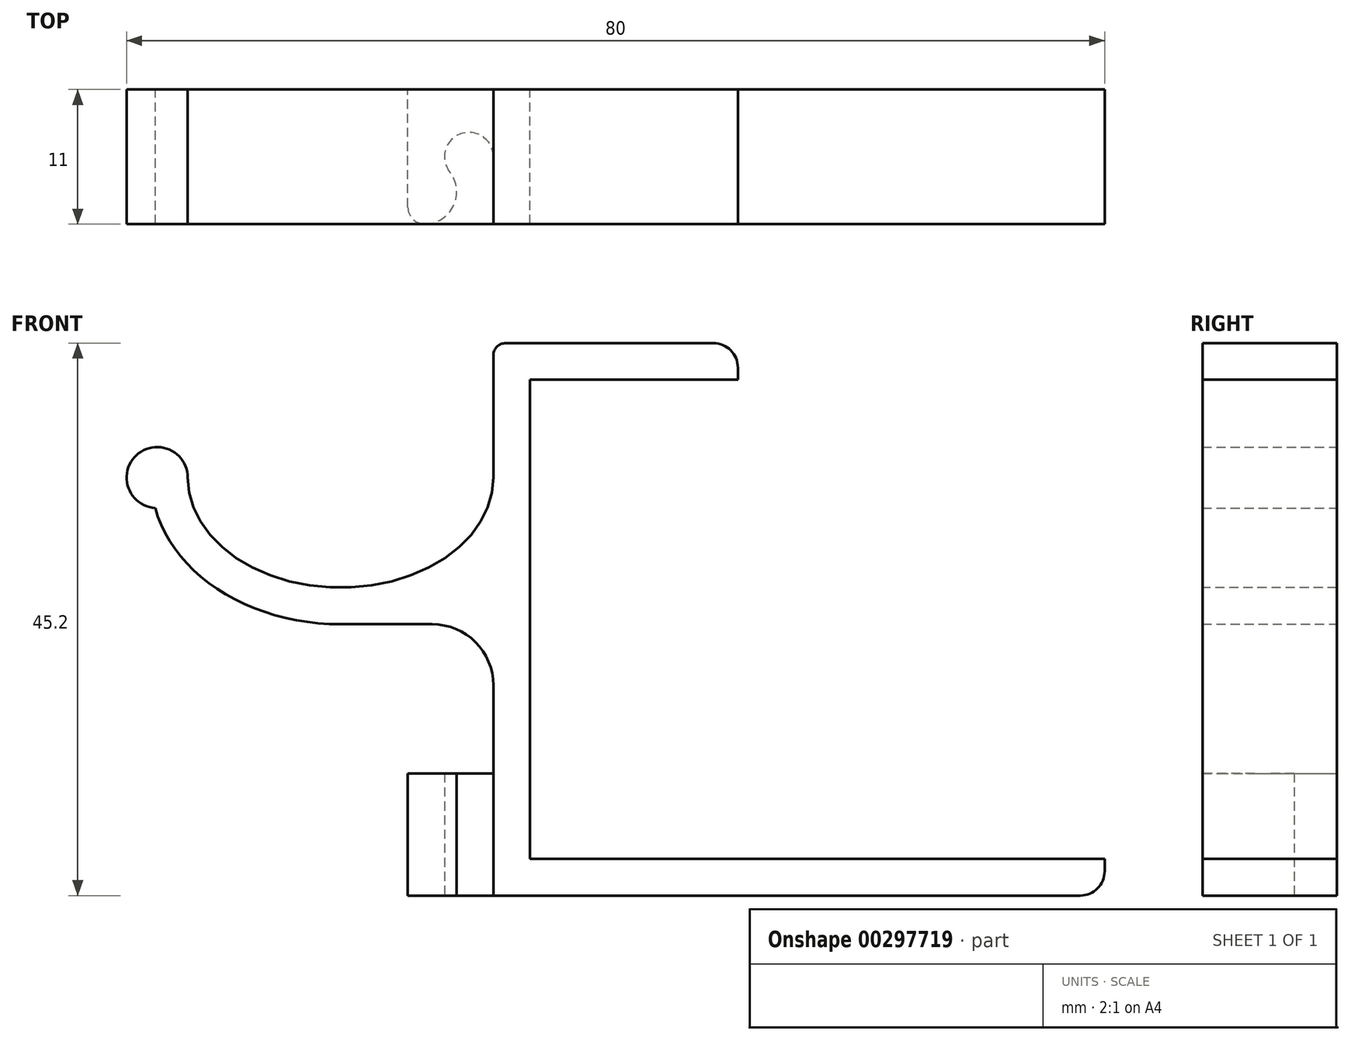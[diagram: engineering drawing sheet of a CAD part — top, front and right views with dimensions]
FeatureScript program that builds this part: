
annotation { "Feature Type Name" : "Feature", "Feature Type Description" : "" }
export const myFeature = defineFeature(function(context is Context, id is Id, definition is map)
    precondition{}
    {
        {
            var Q0;
            Q0=qCreatedBy(makeId("Front.planeOp"),FACE);
            var sketch = newSketch(context, id + "F0", { "sketchPlane" : qUnion([Q0])});
            skLineSegment(sketch, "E0.bottom", {"start": v(0, 0) * mm, "end": v(47, 0) * mm});
            skLineSegment(sketch, "E0.top", {"start": v(0, 39.2) * mm, "end": v(17, 39.2) * mm});
            skLineSegment(sketch, "E0.left", {"start": v(0, 0) * mm, "end": v(0, 39.2) * mm});
            skLineSegment(sketch, "E1.bottom", {"start": v(-2, 42.2) * mm, "end": v(15, 42.2) * mm});
            skLineSegment(sketch, "E1.top", {"start": v(-2, -3) * mm, "end": v(45, -3) * mm});
            skLineSegment(sketch, "E1.left", {"start": v(-3, 41.2) * mm, "end": v(-3, 31.2) * mm});
            skArc(sketch, "E2", {"start": v(0, 42.2) * mm, "mid": v(-2.12, 41.32) * mm, "end": v(-3, 39.2) * mm, "construction": true});
            skArc(sketch, "E3", {"start": v(-3, 0) * mm, "mid": v(-2.12, -2.12) * mm, "end": v(0, -3) * mm, "construction": true});
            skLineSegment(sketch, "E4", {"start": v(17, 39.2) * mm, "end": v(17, 40.2) * mm});
            skLineSegment(sketch, "E5", {"start": v(47, 0) * mm, "end": v(47, -1) * mm});
            skPoint(sketch, "E6.visualSharp", {"position": v(17, 42.2) * mm});
            skArc(sketch, "E6.filletArc", {"start": v(17, 40.2) * mm, "mid": v(16.41, 41.61) * mm, "end": v(15, 42.2) * mm});
            skPoint(sketch, "E7.visualSharp", {"position": v(47, -3) * mm});
            skArc(sketch, "E7.filletArc", {"start": v(45, -3) * mm, "mid": v(46.41, -2.41) * mm, "end": v(47, -1) * mm});
            skPoint(sketch, "E8.visualSharp", {"position": v(-3, 42.2) * mm});
            skArc(sketch, "E8.filletArc", {"start": v(-2, 42.2) * mm, "mid": v(-2.7, 41.9) * mm, "end": v(-3, 41.2) * mm});
            skPoint(sketch, "E9.visualSharp", {"position": v(-3, -3) * mm});
            skArc(sketch, "E9.filletArc", {"start": v(-3, -2) * mm, "mid": v(-2.7, -2.7) * mm, "end": v(-2, -3) * mm});
            skEllipticalArc(sketch, "E10", {});
            skEllipticalArc(sketch, "E11", {});
            skArc(sketch, "E12", {"start": v(-28, 31.2) * mm, "mid": v(-32.2, 33.02) * mm, "end": v(-30.66, 28.7) * mm});
            skLineSegment(sketch, "E13", {"start": v(-15.5, 19.2) * mm, "end": v(-8, 19.2) * mm});
            skLineSegment(sketch, "E14", {"start": v(-15.5, 22.2) * mm, "end": v(-3, 22.2) * mm, "construction": true});
            skArc(sketch, "E15", {"start": v(-3, 14.2) * mm, "mid": v(-4.46, 17.74) * mm, "end": v(-8, 19.2) * mm});
            skLineSegment(sketch, "E16.trimOffspring", {"start": v(-3, 14.2) * mm, "end": v(-3, -2) * mm});
            skLineSegment(sketch, "E17", {"start": v(-3, 31.2) * mm, "end": v(-3, 14.2) * mm, "construction": true});
            const initialGuessF0  = {"E10": [-0.0155, 0.0312, 1, 0, 0.0125, 0.009, 3.141592653589793, 0], "E11": [-0.0155, 0.0312, 1, 0, 0.0155, 0.012, 3.351019286650593, 4.71238898038469]};
            skSetInitialGuess(sketch, initialGuessF0);
            skSolve(sketch);
        }
        {
            var Q0;
            Q0=makeQuery(id+"F0.imprint","IMPRINT",FACE,{"disambiguationData":[TD([[makeQuery(id+"F0.imprint","IMPRINT",EDGE,{"derivedFrom":sQuery(id+"F0.wireOp",EDGE,"E0.bottom")}),-1.0]])]});
            extrude(context, id + "F1", {"entities" : qUnion([Q0]), "depth" : 11 * mm});
        }
        {
            var Q0;
            Q0=makeQuery(id+"F1.opExtrude","SWEPT_FACE",FACE,{"disambiguationData":[OSD([sQuery(id+"F0.wireOp",EDGE,"E1.top")])]});
            var sketch = newSketch(context, id + "F2", { "sketchPlane" : qUnion([Q0])});
            skArc(sketch, "E18", {"start": v(-6.57, 6.74) * mm, "mid": v(-5.66, 3.61) * mm, "end": v(-3, 5.5) * mm});
            skLineSegment(sketch, "E19", {"start": v(-10, 0) * mm, "end": v(-2, 0) * mm});
            skLineSegment(sketch, "E20", {"start": v(-2, 0) * mm, "end": v(-2, 11) * mm});
            skLineSegment(sketch, "E21", {"start": v(-10, 9.63) * mm, "end": v(-10, 0) * mm});
            skLineSegment(sketch, "E22", {"start": v(-3, 5.5) * mm, "end": v(-3, 11) * mm});
            skLineSegment(sketch, "E23", {"start": v(-3, 11) * mm, "end": v(-2, 11) * mm});
            skArc(sketch, "E24", {"start": v(-6.57, 6.74) * mm, "mid": v(-6.26, 9.52) * mm, "end": v(-8.63, 11) * mm});
            skArc(sketch, "E25", {"start": v(-3, 5.5) * mm, "mid": v(-4.34, 7.39) * mm, "end": v(-6.57, 6.74) * mm, "construction": true});
            skArc(sketch, "E26.filletArc", {"start": v(-8.63, 11) * mm, "mid": v(-9.6, 10.6) * mm, "end": v(-10, 9.63) * mm});
            skSolve(sketch);
        }
        {
            var Q0;
            Q0=makeQuery(id+"F2.imprint","IMPRINT",FACE,{"disambiguationData":[TD([[makeQuery(id+"F2.imprint","IMPRINT",EDGE,{"derivedFrom":sQuery(id+"F2.wireOp",EDGE,"E18")}),-1.0]])]});
            extrude(context, id + "F3", {"entities" : qUnion([Q0]), "operationType" : NewBodyOperationType.ADD, "oppositeDirection" : true, "depth" : 10 * mm});
        }
    });
